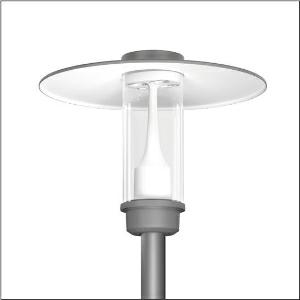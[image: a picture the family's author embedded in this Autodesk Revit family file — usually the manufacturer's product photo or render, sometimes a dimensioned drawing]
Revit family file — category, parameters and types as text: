
# Revit family: litepole_2_iq___p1_0a_5xa5425nf14h_2791
name_source: partatom
category: Lighting Fixtures
units: mm (PartAtom-declared; Revit-internal decimal feet)

## family parameters
Cut with Voids When Loaded = No
Host = Face
Light Source = No
Part Type = Normal
Room Calculation Point = No
Round Connector Dimension = Use Diameter
Shared = No

## types (1)
- --- (1 x LED, 1520 lm, 11.8 W, 2700K)
    Apparent Load = 12 VA
    CIE Flux Codes = 33 62 89 96 100
    Color Rendering = 70
    Color Temperature = 2700K
    Default Elevation = 1800 mm
    Description = Litepole 2 iQ, mast luminaire, Module 540 iQ-SR, primary light control with 3 zone facetted reflector, of plastic, silver coated, highly specular, structured, primary optical cover: cover, of PMMA, transparent, light distribution: P1.0a, light emission: direct distribution, primary light characteristic: strongly asymmetric, installation type: post-top, LED, High Power LED, rated luminous flux: 1.520lm, luminous efficacy: 129lm/W, light colour: 727, colour temperature: 2700K, control gear: ECG iQ, control: pre-setting: logarithmic dimming characteristic, Street-Remote, Auto-Match, Temp-Guard, Lumen-Switch, Night-Set, Smart-Wire, Light-Fading, Desk-Remote (wireless, voltage-free reading and setting of iQ features in the workshop via application-optimized NFC function/RFID function), optimised constant luminous flux control (CLO 2.0), with terminal, 6-pole, max. 2.5mm², mains connection: 230..240V, AC, 50/60Hz, start of lifetime: 12W, end of service life: 12W, reduction: 6W, luminaire housing, upper part, of aluminium, coated, Siteco® metallic grey (DB 702S), diameter: 750mm, height: 590mm, spigot size: d x l = 76 x 70mm (post-top) | with reducer (optional accessory) 60 x 70mm, post-top mast mounting element, of diecast aluminium, coated, Siteco® metallic grey (DB 702S), Module 540 iQ-SR, traffic white (RAL 9016), equipment: standard, protection rating (complete): IP65, insulation class (complete): insulation class II (safety insulation), certification: CE, ENEC, VDE, packaging unit: 1 piece

Light Distribution: P1.0a
    Height = 590 mm
    Lamp = 1 x LED
    Lamp Light Flux = 1520 lm
    Lamp Power = 11.8 W
    Lamp count = 1
    Length = 750 mm
    Luminous efficacy = 129 lm/W
    Manufacturer = Siteco
    ModVariant = No
    Model = 5XA5425NF14H
    Number of Poles = 1
    OnlyDefault = Yes
    Power Factor = 1
    Product Name = Litepole 2 iQ | P1.0a
    Product group = mast luminaire | pylon top
    ProductGroupID = 6100
    Protection Class = Protection class II
    Protection Degree = IP 65
    RLX_Detail_Level = 1
    RLX_Emergency_Light_Flux = 0 lm
    RLX_Emergency_Type = 0
    RLX_Emergency_Type_DB = No
    RlxData = <blob elided: 138225 chars, md5=e58c98ed>
    Socket = socket
    Standby Power = 0 W
    System Light Flux = 1520 lm
    System Power = 12 W
    Type Comments = factory setting: luminous flux: 100 % | dim-lin: 254 | 472 mA
    Type Image = l_1006518.jpg
    URL = http://relux.com
    VarID = @adj_122773
    Voltage = 0 V
    Weight = 0.00 kg
    Width = 0 mm  [stored 0 ft]

note: [stored X ft] marks values corroborated as IEEE doubles in the binary element streams (Revit-internal decimal feet)

## geometry (parser evidence)
native form markers: Blend x4, Sweep x10
no freeform markers — native parametric forms only
